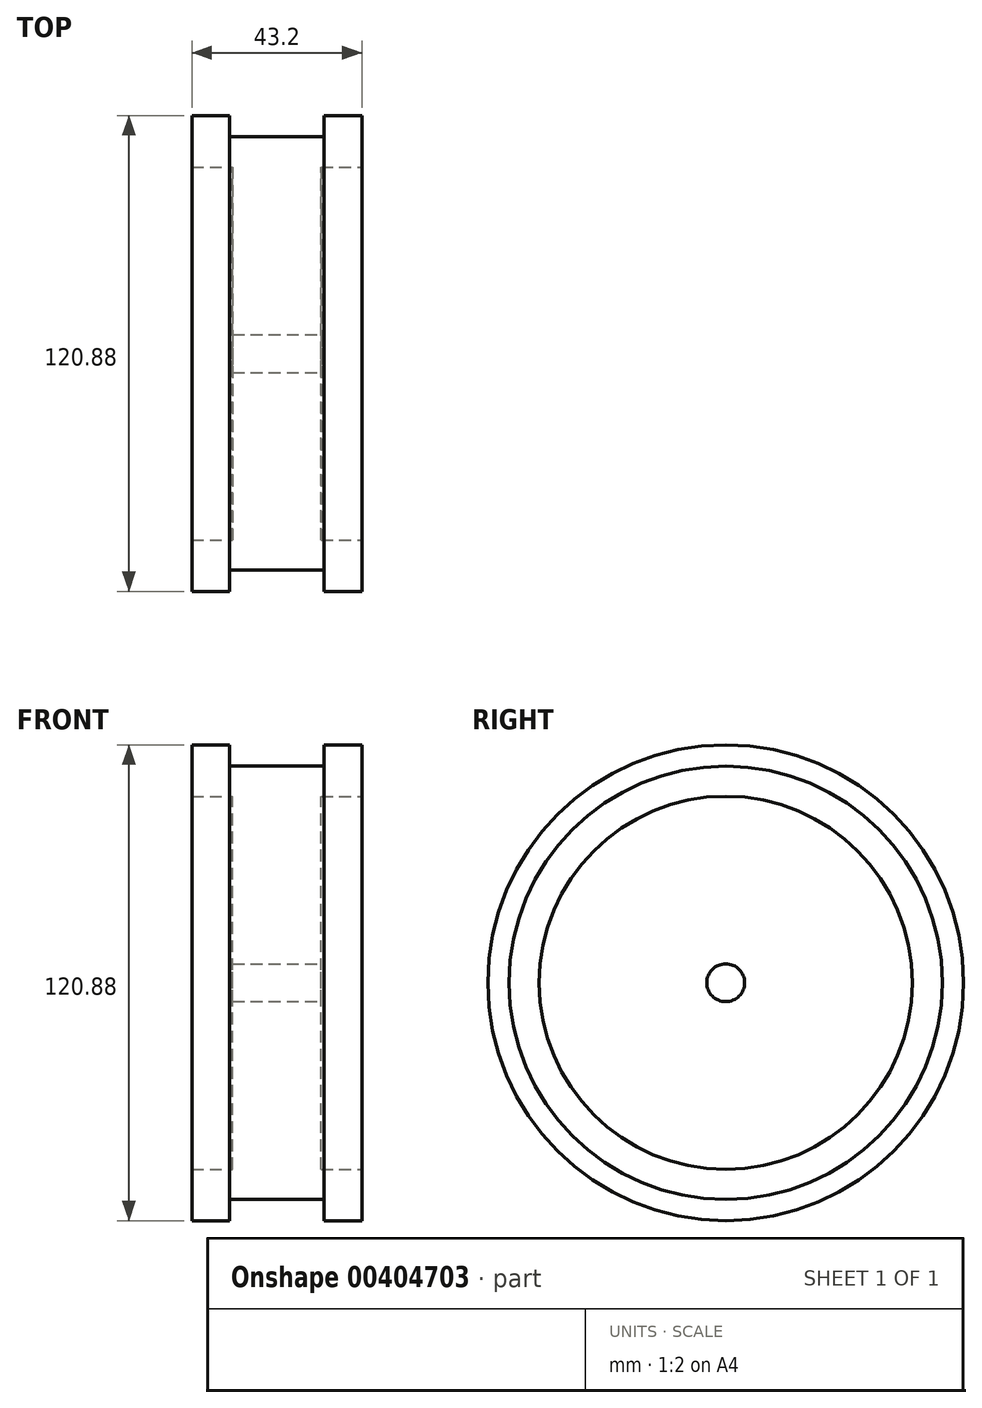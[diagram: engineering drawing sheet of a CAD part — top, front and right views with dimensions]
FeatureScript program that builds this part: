
annotation { "Feature Type Name" : "Feature", "Feature Type Description" : "" }
export const myFeature = defineFeature(function(context is Context, id is Id, definition is map)
    precondition{}
    {
        {
            var Q0;
            Q0=qCreatedBy(makeId("Front.planeOp"),FACE);
            var sketch = newSketch(context, id + "F0", { "sketchPlane" : qUnion([Q0])});
            skLineSegment(sketch, "E0", {"start": v(-11.25, 47.4) * mm, "end": v(-11.25, 4.8) * mm});
            skLineSegment(sketch, "E1", {"start": v(-11.25, 4.8) * mm, "end": v(0, 4.8) * mm});
            skLineSegment(sketch, "E2", {"start": v(-21.6, 47.4) * mm, "end": v(-11.25, 47.4) * mm});
            skLineSegment(sketch, "E3", {"start": v(-21.6, 60.44) * mm, "end": v(-21.6, 47.4) * mm});
            skLineSegment(sketch, "E4", {"start": v(-21.6, 60.44) * mm, "end": v(-12, 60.44) * mm});
            skLineSegment(sketch, "E5", {"start": v(-12, 60.44) * mm, "end": v(-12, 55.04) * mm});
            skLineSegment(sketch, "E6", {"start": v(-12, 55.04) * mm, "end": v(0, 55.04) * mm});
            skLineSegment(sketch, "E7", {"start": v(0, 73.04) * mm, "end": v(0, -39.3) * mm});
            skLineSegment(sketch, "E8.MirrorCS", {"start": v(12, 55.04) * mm, "end": v(0, 55.04) * mm});
            skLineSegment(sketch, "E9.MirrorCS", {"start": v(12, 60.44) * mm, "end": v(12, 55.04) * mm});
            skLineSegment(sketch, "E10.MirrorCS", {"start": v(11.25, 47.4) * mm, "end": v(11.25, 4.8) * mm});
            skLineSegment(sketch, "E11.MirrorCS", {"start": v(11.25, 4.8) * mm, "end": v(0, 4.8) * mm});
            skLineSegment(sketch, "E12.MirrorCS", {"start": v(21.6, 47.4) * mm, "end": v(11.25, 47.4) * mm});
            skLineSegment(sketch, "E13.MirrorCS", {"start": v(21.6, 60.44) * mm, "end": v(21.6, 47.4) * mm});
            skLineSegment(sketch, "E14.MirrorCS", {"start": v(21.6, 60.44) * mm, "end": v(12, 60.44) * mm});
            skSolve(sketch);
        }
        {
            var Q0;
            Q0=qCreatedBy(makeId("Front.planeOp"),FACE);
            var sketch = newSketch(context, id + "F1", { "sketchPlane" : qUnion([Q0])});
            skLineSegment(sketch, "E15", {"start": v(0, 0) * mm, "end": v(43.38, 0) * mm});
            skSolve(sketch);
        }
        {
            var Q0;
            Q0=makeQuery(id+"F0.imprint","IMPRINT",FACE,{"disambiguationData":[TD([[makeQuery(id+"F0.imprint","IMPRINT",EDGE,{"derivedFrom":sQuery(id+"F0.wireOp",EDGE,"E0")}),1.0]])]});
            var Q1;
            {var subQ0=sQuery(id+"F0.wireOp",EDGE,"E8.MirrorCS");Q1=makeQuery(id+"F0.imprint","IMPRINT",FACE,{"disambiguationData":[TD([[makeQuery(id+"F0.imprint","IMPRINT",EDGE,{"derivedFrom":subQ0}),1.0]])]});}
            var Q2;
            Q2=sQuery(id+"F0.wireOp",EDGE,"E10.MirrorCS");
            var Q3;
            Q3=sQuery(id+"F0.wireOp",EDGE,"E12.MirrorCS");
            var Q4;
            Q4=sQuery(id+"F0.wireOp",EDGE,"E13.MirrorCS");
            var Q5;
            Q5=sQuery(id+"F0.wireOp",EDGE,"E14.MirrorCS");
            var Q6;
            Q6=sQuery(id+"F0.wireOp",EDGE,"E9.MirrorCS");
            var Q7;
            Q7=sQuery(id+"F0.wireOp",EDGE,"E8.MirrorCS");
            var Q8;
            Q8=sQuery(id+"F0.wireOp",EDGE,"E6");
            var Q9;
            Q9=sQuery(id+"F0.wireOp",EDGE,"E5");
            var Q10;
            Q10=sQuery(id+"F0.wireOp",EDGE,"E4");
            var Q11;
            Q11=sQuery(id+"F0.wireOp",EDGE,"E3");
            var Q12;
            Q12=sQuery(id+"F0.wireOp",EDGE,"E2");
            var Q13;
            Q13=sQuery(id+"F0.wireOp",EDGE,"E0");
            var Q14;
            Q14=sQuery(id+"F0.wireOp",EDGE,"E1");
            var Q15;
            Q15=sQuery(id+"F0.wireOp",EDGE,"E11.MirrorCS");
            var Q16;
            Q16=sQuery(id+"F1.wireOp",EDGE,"E15");
            revolve(context, id + "F2", {"bodyType" : ToolBodyType.SURFACE, "entities" : qUnion([Q0, Q1]), "surfaceEntities" : qUnion([Q2, Q3, Q4, Q5, Q6, Q7, Q8, Q9, Q10, Q11, Q12, Q13, Q14, Q15]), "axis" : qUnion([Q16]), "revolveType" : RevolveType.FULL});
        }
    });
